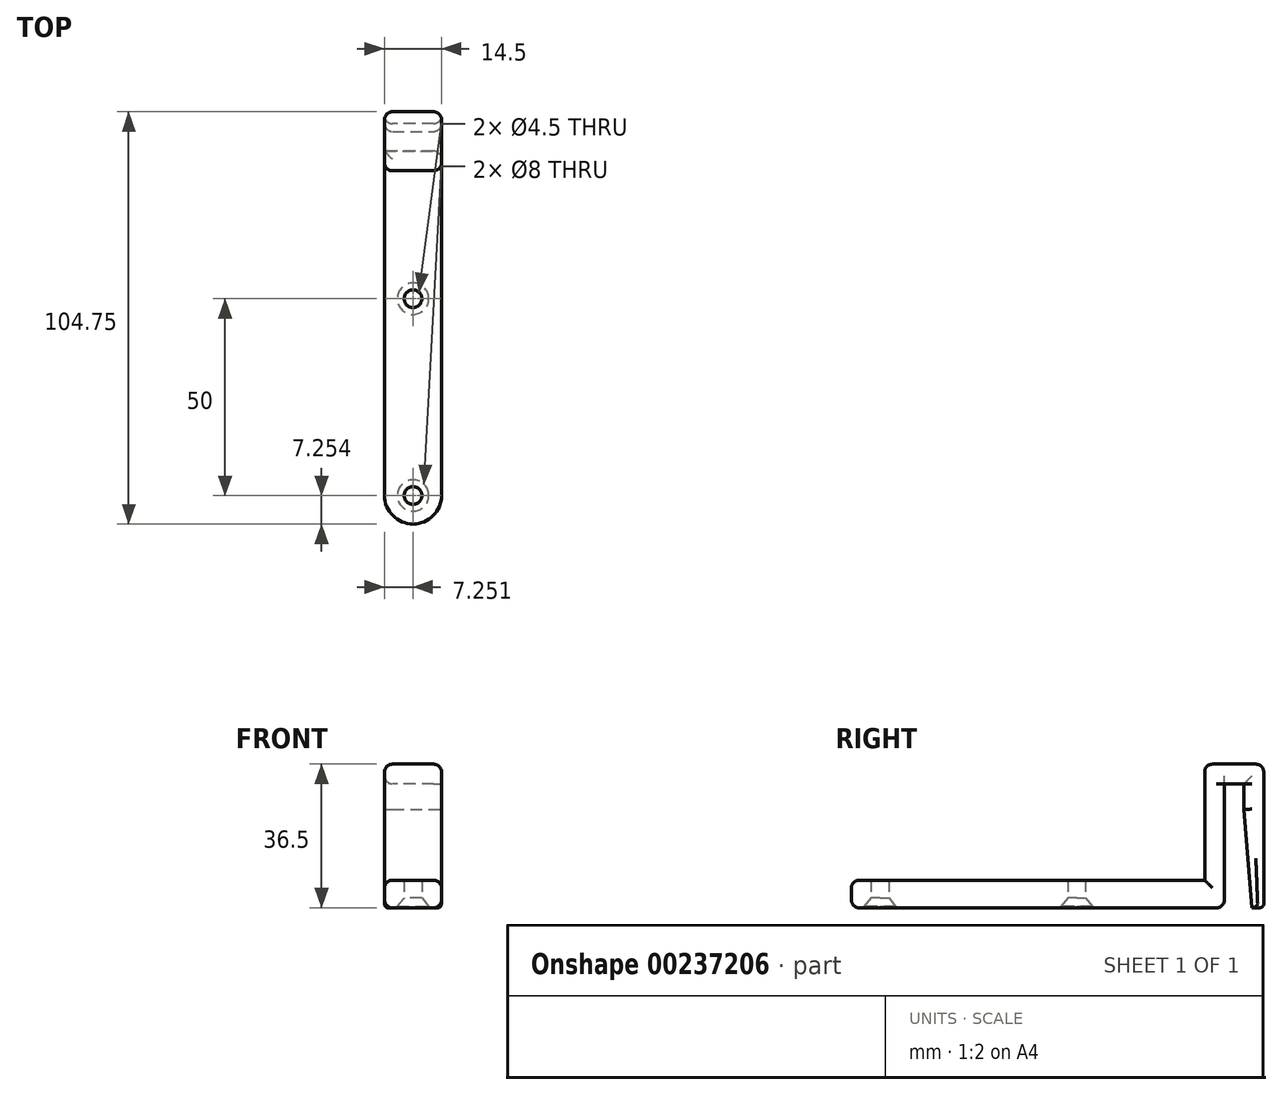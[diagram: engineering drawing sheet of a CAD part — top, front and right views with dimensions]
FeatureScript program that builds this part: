
annotation { "Feature Type Name" : "Feature", "Feature Type Description" : "" }
export const myFeature = defineFeature(function(context is Context, id is Id, definition is map)
    precondition{}
    {
        {
            assignVariable(context, id + "F0", {"name" : "M4_clearance_diameter", "anyValue" : 4.5});
        }
        {
            assignVariable(context, id + "F1", {"name" : "side_thickness", "anyValue" : 5});
        }
        {
            var Q0;
            Q0=qCreatedBy(makeId("Top.planeOp"),FACE);
            var sketch = newSketch(context, id + "F2", { "sketchPlane" : qUnion([Q0])});
            skCircle(sketch, "E0", {"center": v(-10.53, -5.15) * mm, "radius": 2.25 * mm});
            skLineSegment(sketch, "E1.bottom", {"start": v(-17.78, 52.1) * mm, "end": v(-3.28, 52.1) * mm});
            skLineSegment(sketch, "E1.top", {"start": v(-17.78, -12.4) * mm, "end": v(-3.28, -12.4) * mm});
            skLineSegment(sketch, "E1.left", {"start": v(-17.78, 52.1) * mm, "end": v(-17.78, -12.4) * mm});
            skLineSegment(sketch, "E1.right", {"start": v(-3.28, 52.1) * mm, "end": v(-3.28, -12.4) * mm});
            skCircle(sketch, "E2", {"center": v(-10.53, 44.85) * mm, "radius": 2.25 * mm});
            skCircle(sketch, "E3", {"center": v(-10.53, -5.15) * mm, "radius": 7.25 * mm});
            skSolve(sketch);
        }
        {
            assignVariable(context, id + "F3", {"name" : "hole_depth_psu", "anyValue" : 3});
        }
        {
            assignVariable(context, id + "F4", {"name" : "screw_length", "anyValue" : 7.5});
        }
        {
            assignVariable(context, id + "F5", {"name" : "screw_head_length", "anyValue" : 2.5});
        }
        {
            assignVariable(context, id + "F6", {"name" : "bracket_thickness", "anyValue" : getVariable(context, 'screw_length') + getVariable(context, 'screw_head_length') - getVariable(context, 'hole_depth_psu')});
        }
        {
            var Q0;
            {var subQ0=sQuery(id+"F2.wireOp",EDGE,"E1.bottom");Q0=makeQuery(id+"F2.imprint","IMPRINT",FACE,{"disambiguationData":[TD([[makeQuery(id+"F2.imprint","IMPRINT",EDGE,{"derivedFrom":subQ0}),-1.0]])]});}
            var Q1;
            Q1=makeQuery(id+"F2.imprint","IMPRINT",FACE,{"disambiguationData":[TD([[makeQuery(id+"F2.imprint","IMPRINT",EDGE,{"derivedFrom":sQuery(id+"F2.wireOp",EDGE,"E0")}),-1.0]])]});
            extrude(context, id + "F7", {"entities" : qUnion([Q0, Q1]), "depth" : (getVariable(context, 'bracket_thickness')) * mm});
        }
        {
            assignVariable(context, id + "F8", {"name" : "screw_head_diameter", "anyValue" : 8});
        }
        {
            assignVariable(context, id + "F9", {"name" : "screw_head_chamfer", "anyValue" : getVariable(context, 'screw_head_length') - 0.4});
        }
        {
            var Q0;
            Q0=makeQuery(id+"F7.opExtrude","CAP_FACE",FACE,{"disambiguationData":[OSD([sQuery(id+"F2.wireOp",EDGE,"E0"),sQuery(id+"F2.wireOp",EDGE,"E1.bottom"),sQuery(id+"F2.wireOp",EDGE,"E1.left"),sQuery(id+"F2.wireOp",EDGE,"E1.right"),sQuery(id+"F2.wireOp",EDGE,"E2"),sQuery(id+"F2.wireOp",EDGE,"E3")])],"isStart":true});
            var sketch = newSketch(context, id + "F10", { "sketchPlane" : qUnion([Q0])});
            skCircle(sketch, "E4", {"center": v(-10.53, 5.15) * mm, "radius": 4 * mm});
            skCircle(sketch, "E5", {"center": v(-10.53, -44.85) * mm, "radius": 4 * mm});
            skSolve(sketch);
        }
        {
            var Q0;
            Q0=makeQuery(id+"F10.imprint","IMPRINT",FACE,{"disambiguationData":[TD([[makeQuery(id+"F10.imprint","IMPRINT",EDGE,{"derivedFrom":sQuery(id+"F10.wireOp",EDGE,"E4")}),1.0]])]});
            var Q1;
            Q1=makeQuery(id+"F10.imprint","IMPRINT",FACE,{"disambiguationData":[TD([[makeQuery(id+"F10.imprint","IMPRINT",EDGE,{"derivedFrom":sQuery(id+"F10.wireOp",EDGE,"E5")}),1.0]])]});
            extrude(context, id + "F11", {"entities" : qUnion([Q0, Q1]), "operationType" : NewBodyOperationType.REMOVE, "oppositeDirection" : true, "depth" : (getVariable(context, 'screw_head_length')) * mm});
        }
        {
            var Q0;
            Q0=makeQuery(id+"F11.boolean.opBoolean","COPY",EDGE,{"derivedFrom":makeQuery(id+"F11.opExtrude","CAP_EDGE",EDGE,{"disambiguationData":[OSD([sQuery(id+"F10.wireOp",EDGE,"E4")])],"isStart":false})});
            var Q1;
            Q1=makeQuery(id+"F11.boolean.opBoolean","COPY",EDGE,{"derivedFrom":makeQuery(id+"F11.opExtrude","CAP_EDGE",EDGE,{"disambiguationData":[OSD([sQuery(id+"F10.wireOp",EDGE,"E5")])],"isStart":false})});
            chamfer(context, id + "F12", {"entities" : qUnion([Q0, Q1]), "chamferType" : ChamferType.TWO_OFFSETS, "width1" : ((getVariable(context, 'screw_head_diameter') - getVariable(context, 'M4_clearance_diameter')) / 2) * mm, "oppositeDirection" : false, "width2" : (getVariable(context, 'screw_head_chamfer')) * mm, "tangentPropagation" : true});
        }
        {
            assignVariable(context, id + "F13", {"name" : "bracket_height", "anyValue" : 36.5});
        }
        {
            var Q0;
            Q0=makeQuery(id+"F7.opExtrude","CAP_FACE",FACE,{"disambiguationData":[OSD([sQuery(id+"F2.wireOp",EDGE,"E0"),sQuery(id+"F2.wireOp",EDGE,"E1.bottom"),sQuery(id+"F2.wireOp",EDGE,"E1.left"),sQuery(id+"F2.wireOp",EDGE,"E1.right"),sQuery(id+"F2.wireOp",EDGE,"E2"),sQuery(id+"F2.wireOp",EDGE,"E3")])],"isStart":false});
            var sketch = newSketch(context, id + "F14", { "sketchPlane" : qUnion([Q0])});
            skLineSegment(sketch, "E6.bottom", {"start": v(-17.78, 44.85) * mm, "end": v(-3.28, 44.85) * mm});
            skLineSegment(sketch, "E6.top", {"start": v(-17.78, 77.35) * mm, "end": v(-3.28, 77.35) * mm});
            skLineSegment(sketch, "E6.left", {"start": v(-17.78, 44.85) * mm, "end": v(-17.78, 77.35) * mm});
            skLineSegment(sketch, "E6.right", {"start": v(-3.28, 44.85) * mm, "end": v(-3.28, 77.35) * mm});
            skPoint(sketch, "E7", {"position": v(-10.53, 44.85) * mm});
            skSolve(sketch);
        }
        {
            var Q0;
            {var subQ0=sQuery(id+"F14.wireOp",EDGE,"E6.top");Q0=makeQuery(id+"F14.imprint","IMPRINT",FACE,{"disambiguationData":[TD([[makeQuery(id+"F14.imprint","IMPRINT",EDGE,{"derivedFrom":subQ0}),-1.0]])]});}
            extrude(context, id + "F15", {"entities" : qUnion([Q0]), "operationType" : NewBodyOperationType.ADD, "oppositeDirection" : true, "depth" : (getVariable(context, 'bracket_thickness')) * mm});
        }
        {
            var Q0;
            Q0=makeQuery(id+"F15.opExtrude","SWEPT_FACE",FACE,{"disambiguationData":[OSD([sQuery(id+"F14.wireOp",EDGE,"E6.top")])]});
            var sketch = newSketch(context, id + "F16", { "sketchPlane" : qUnion([Q0])});
            skLineSegment(sketch, "E8.bottom", {"start": v(3.28, 0) * mm, "end": v(17.78, 0) * mm});
            skLineSegment(sketch, "E8.top", {"start": v(3.28, 36.5) * mm, "end": v(17.78, 36.5) * mm});
            skLineSegment(sketch, "E8.left", {"start": v(3.28, 0) * mm, "end": v(3.28, 36.5) * mm});
            skLineSegment(sketch, "E8.right", {"start": v(17.78, 0) * mm, "end": v(17.78, 36.5) * mm});
            skSolve(sketch);
        }
        {
            var Q0;
            {var subQ0=sQuery(id+"F16.wireOp",EDGE,"E8.top");Q0=makeQuery(id+"F16.imprint","IMPRINT",FACE,{"disambiguationData":[TD([[makeQuery(id+"F16.imprint","IMPRINT",EDGE,{"derivedFrom":subQ0}),-1.0]])]});}
            var Q1;
            {var subQ0=sQuery(id+"F16.wireOp",EDGE,"E8.bottom");Q1=makeQuery(id+"F16.imprint","IMPRINT",FACE,{"disambiguationData":[TD([[makeQuery(id+"F16.imprint","IMPRINT",EDGE,{"derivedFrom":subQ0}),-1.0]])]});}
            extrude(context, id + "F17", {"entities" : qUnion([Q0, Q1]), "operationType" : NewBodyOperationType.ADD, "depth" : (getVariable(context, 'side_thickness')) * mm});
        }
        {
            var Q0;
            Q0=makeQuery(id+"F17.opExtrude","CAP_FACE",FACE,{"disambiguationData":[OSD([sQuery(id+"F16.wireOp",EDGE,"E8.bottom"),sQuery(id+"F16.wireOp",EDGE,"E8.top"),sQuery(id+"F16.wireOp",EDGE,"E8.left"),sQuery(id+"F16.wireOp",EDGE,"E8.right")])],"isStart":false});
            var sketch = newSketch(context, id + "F18", { "sketchPlane" : qUnion([Q0])});
            skLineSegment(sketch, "E9.bottom", {"start": v(3.28, 36.5) * mm, "end": v(17.78, 36.5) * mm});
            skLineSegment(sketch, "E9.top", {"start": v(3.28, 31.5) * mm, "end": v(17.78, 31.5) * mm});
            skLineSegment(sketch, "E9.left", {"start": v(3.28, 36.5) * mm, "end": v(3.28, 31.5) * mm});
            skLineSegment(sketch, "E9.right", {"start": v(17.78, 36.5) * mm, "end": v(17.78, 31.5) * mm});
            skSolve(sketch);
        }
        {
            var Q0;
            Q0=makeQuery(id+"F18.imprint","IMPRINT",FACE,{"disambiguationData":[TD([[makeQuery(id+"F18.imprint","IMPRINT",EDGE,{"derivedFrom":sQuery(id+"F18.wireOp",EDGE,"E9.bottom")}),-1.0]])]});
            extrude(context, id + "F19", {"entities" : qUnion([Q0]), "operationType" : NewBodyOperationType.ADD, "depth" : 10 * mm});
        }
        {
            var Q0;
            Q0=makeQuery(id+"F19.opExtrude","SWEPT_FACE",FACE,{"disambiguationData":[OSD([sQuery(id+"F18.wireOp",EDGE,"E9.top")])]});
            var sketch = newSketch(context, id + "F20", { "sketchPlane" : qUnion([Q0])});
            skLineSegment(sketch, "E10.bottom", {"start": v(-17.78, -92.35) * mm, "end": v(-3.28, -92.35) * mm});
            skLineSegment(sketch, "E10.top", {"start": v(-17.78, -87.35) * mm, "end": v(-3.28, -87.35) * mm});
            skLineSegment(sketch, "E10.left", {"start": v(-17.78, -92.35) * mm, "end": v(-17.78, -87.35) * mm});
            skLineSegment(sketch, "E10.right", {"start": v(-3.28, -92.35) * mm, "end": v(-3.28, -87.35) * mm});
            skSolve(sketch);
        }
        {
            var Q0;
            Q0=makeQuery(id+"F20.imprint","IMPRINT",FACE,{"disambiguationData":[TD([[makeQuery(id+"F20.imprint","IMPRINT",EDGE,{"derivedFrom":sQuery(id+"F20.wireOp",EDGE,"E10.bottom")}),-1.0]])]});
            extrude(context, id + "F21", {"entities" : qUnion([Q0]), "operationType" : NewBodyOperationType.ADD, "depth" : (getVariable(context, 'bracket_height') - 5) * mm});
        }
        {
            var Q0;
            Q0=makeQuery(id+"F21.opExtrude","CAP_EDGE",EDGE,{"disambiguationData":[OSD([sQuery(id+"F20.wireOp",EDGE,"E10.top")])],"isStart":false});
            chamfer(context, id + "F22", {"entities" : qUnion([Q0]), "chamferType" : ChamferType.TWO_OFFSETS, "width1" : 25 * mm, "oppositeDirection" : false, "width2" : 2 * mm, "tangentPropagation" : true});
        }
        {
            var Q0;
            Q0=makeQuery(id+"F19.boolean.opBoolean","MERGE",EDGE,{"derivedFrom":[makeQuery(id+"F17.opExtrude","SWEPT_EDGE",EDGE,{"disambiguationData":[OSD([sQuery(id+"F16.wireOp",EDGE,"E8.top"),sQuery(id+"F16.wireOp",EDGE,"E8.left")])]}),makeQuery(id+"F19.opExtrude","SWEPT_EDGE",EDGE,{"disambiguationData":[OSD([sQuery(id+"F18.wireOp",EDGE,"E9.bottom"),sQuery(id+"F18.wireOp",EDGE,"E9.left")])]})]});
            var Q1;
            Q1=makeQuery(id+"F17.opExtrude","CAP_EDGE",EDGE,{"disambiguationData":[OSD([sQuery(id+"F16.wireOp",EDGE,"E8.left")])],"isStart":true});
            var Q2;
            Q2=makeQuery(id+"F17.opExtrude","CAP_EDGE",EDGE,{"disambiguationData":[OSD([sQuery(id+"F16.wireOp",EDGE,"E8.left")])],"isStart":false});
            var Q3;
            Q3=makeQuery(id+"F21.opExtrude","SWEPT_EDGE",EDGE,{"disambiguationData":[OSD([sQuery(id+"F16.wireOp",EDGE,"E8.left"),sQuery(id+"F18.wireOp",EDGE,"E9.top"),sQuery(id+"F18.wireOp",EDGE,"E9.left"),sQuery(id+"F20.wireOp",EDGE,"E10.top"),sQuery(id+"F20.wireOp",EDGE,"E10.right")])]});
            var Q4;
            Q4=makeQuery(id+"F21.boolean.opBoolean","MERGE",EDGE,{"derivedFrom":[makeQuery(id+"F19.opExtrude","CAP_EDGE",EDGE,{"disambiguationData":[OSD([sQuery(id+"F18.wireOp",EDGE,"E9.left")])],"isStart":false}),makeQuery(id+"F21.opExtrude","SWEPT_EDGE",EDGE,{"disambiguationData":[OSD([sQuery(id+"F20.wireOp",EDGE,"E10.bottom"),sQuery(id+"F20.wireOp",EDGE,"E10.right")])]})]});
            var Q5;
            Q5=makeQuery(id+"F22.opChamfer","BLEND_EDGE",EDGE,{"blendedFrom":[makeQuery(id+"F21.opExtrude","CAP_EDGE",EDGE,{"disambiguationData":[OSD([sQuery(id+"F20.wireOp",EDGE,"E10.top")])],"isStart":false}),makeQuery(id+"F21.boolean.opBoolean","MERGE",FACE,{"derivedFrom":[makeQuery(id+"F19.boolean.opBoolean","MERGE",FACE,{"derivedFrom":[makeQuery(id+"F17.boolean.opBoolean","MERGE",FACE,{"derivedFrom":[makeQuery(id+"F15.boolean.opBoolean","MERGE",FACE,{"derivedFrom":[makeQuery(id+"F7.opExtrude","SWEPT_FACE",FACE,{"disambiguationData":[OSD([sQuery(id+"F2.wireOp",EDGE,"E1.right")])]}),makeQuery(id+"F15.opExtrude","SWEPT_FACE",FACE,{"disambiguationData":[OSD([sQuery(id+"F14.wireOp",EDGE,"E6.right")])]})]}),makeQuery(id+"F17.opExtrude","SWEPT_FACE",FACE,{"disambiguationData":[OSD([sQuery(id+"F16.wireOp",EDGE,"E8.left")])]})]}),makeQuery(id+"F19.opExtrude","SWEPT_FACE",FACE,{"disambiguationData":[OSD([sQuery(id+"F18.wireOp",EDGE,"E9.left")])]})]}),makeQuery(id+"F21.opExtrude","SWEPT_FACE",FACE,{"disambiguationData":[OSD([sQuery(id+"F20.wireOp",EDGE,"E10.right")])]})]})],"blendedInto":[makeQuery(id+"F21.boolean.opBoolean","MERGE",FACE,{"derivedFrom":[makeQuery(id+"F19.boolean.opBoolean","MERGE",FACE,{"derivedFrom":[makeQuery(id+"F17.boolean.opBoolean","MERGE",FACE,{"derivedFrom":[makeQuery(id+"F15.boolean.opBoolean","MERGE",FACE,{"derivedFrom":[makeQuery(id+"F7.opExtrude","SWEPT_FACE",FACE,{"disambiguationData":[OSD([sQuery(id+"F2.wireOp",EDGE,"E1.right")])]}),makeQuery(id+"F15.opExtrude","SWEPT_FACE",FACE,{"disambiguationData":[OSD([sQuery(id+"F14.wireOp",EDGE,"E6.right")])]})]}),makeQuery(id+"F17.opExtrude","SWEPT_FACE",FACE,{"disambiguationData":[OSD([sQuery(id+"F16.wireOp",EDGE,"E8.left")])]})]}),makeQuery(id+"F19.opExtrude","SWEPT_FACE",FACE,{"disambiguationData":[OSD([sQuery(id+"F18.wireOp",EDGE,"E9.left")])]})]}),makeQuery(id+"F21.opExtrude","SWEPT_FACE",FACE,{"disambiguationData":[OSD([sQuery(id+"F20.wireOp",EDGE,"E10.right")])]})]})]});
            var Q6;
            Q6=makeQuery(id+"F15.boolean.opBoolean","MERGE",EDGE,{"derivedFrom":[makeQuery(id+"F7.opExtrude","CAP_EDGE",EDGE,{"disambiguationData":[OSD([sQuery(id+"F2.wireOp",EDGE,"E1.right")])],"isStart":false}),makeQuery(id+"F15.opExtrude","CAP_EDGE",EDGE,{"disambiguationData":[OSD([sQuery(id+"F14.wireOp",EDGE,"E6.right")])],"isStart":true})]});
            var Q7;
            Q7=makeQuery(id+"F17.boolean.opBoolean","MERGE",EDGE,{"derivedFrom":[makeQuery(id+"F15.boolean.opBoolean","MERGE",EDGE,{"derivedFrom":[makeQuery(id+"F7.opExtrude","CAP_EDGE",EDGE,{"disambiguationData":[OSD([sQuery(id+"F2.wireOp",EDGE,"E1.right")])],"isStart":true}),makeQuery(id+"F15.opExtrude","CAP_EDGE",EDGE,{"disambiguationData":[OSD([sQuery(id+"F14.wireOp",EDGE,"E6.right")])],"isStart":false})]}),makeQuery(id+"F17.opExtrude","SWEPT_EDGE",EDGE,{"disambiguationData":[OSD([sQuery(id+"F16.wireOp",EDGE,"E8.bottom"),sQuery(id+"F16.wireOp",EDGE,"E8.left")])]})]});
            var Q8;
            Q8=makeQuery(id+"F17.opExtrude","CAP_EDGE",EDGE,{"disambiguationData":[OSD([sQuery(id+"F16.wireOp",EDGE,"E8.right")])],"isStart":true});
            var Q9;
            Q9=makeQuery(id+"F22.opChamfer","BLEND_EDGE",EDGE,{"blendedFrom":[makeQuery(id+"F21.opExtrude","CAP_EDGE",EDGE,{"disambiguationData":[OSD([sQuery(id+"F20.wireOp",EDGE,"E10.top")])],"isStart":false}),makeQuery(id+"F21.boolean.opBoolean","MERGE",FACE,{"derivedFrom":[makeQuery(id+"F19.boolean.opBoolean","MERGE",FACE,{"derivedFrom":[makeQuery(id+"F17.boolean.opBoolean","MERGE",FACE,{"derivedFrom":[makeQuery(id+"F15.boolean.opBoolean","MERGE",FACE,{"derivedFrom":[makeQuery(id+"F7.opExtrude","SWEPT_FACE",FACE,{"disambiguationData":[OSD([sQuery(id+"F2.wireOp",EDGE,"E1.left")])]}),makeQuery(id+"F15.opExtrude","SWEPT_FACE",FACE,{"disambiguationData":[OSD([sQuery(id+"F14.wireOp",EDGE,"E6.left")])]})]}),makeQuery(id+"F17.opExtrude","SWEPT_FACE",FACE,{"disambiguationData":[OSD([sQuery(id+"F16.wireOp",EDGE,"E8.right")])]})]}),makeQuery(id+"F19.opExtrude","SWEPT_FACE",FACE,{"disambiguationData":[OSD([sQuery(id+"F18.wireOp",EDGE,"E9.right")])]})]}),makeQuery(id+"F21.opExtrude","SWEPT_FACE",FACE,{"disambiguationData":[OSD([sQuery(id+"F20.wireOp",EDGE,"E10.left")])]})]})],"blendedInto":[makeQuery(id+"F21.boolean.opBoolean","MERGE",FACE,{"derivedFrom":[makeQuery(id+"F19.boolean.opBoolean","MERGE",FACE,{"derivedFrom":[makeQuery(id+"F17.boolean.opBoolean","MERGE",FACE,{"derivedFrom":[makeQuery(id+"F15.boolean.opBoolean","MERGE",FACE,{"derivedFrom":[makeQuery(id+"F7.opExtrude","SWEPT_FACE",FACE,{"disambiguationData":[OSD([sQuery(id+"F2.wireOp",EDGE,"E1.left")])]}),makeQuery(id+"F15.opExtrude","SWEPT_FACE",FACE,{"disambiguationData":[OSD([sQuery(id+"F14.wireOp",EDGE,"E6.left")])]})]}),makeQuery(id+"F17.opExtrude","SWEPT_FACE",FACE,{"disambiguationData":[OSD([sQuery(id+"F16.wireOp",EDGE,"E8.right")])]})]}),makeQuery(id+"F19.opExtrude","SWEPT_FACE",FACE,{"disambiguationData":[OSD([sQuery(id+"F18.wireOp",EDGE,"E9.right")])]})]}),makeQuery(id+"F21.opExtrude","SWEPT_FACE",FACE,{"disambiguationData":[OSD([sQuery(id+"F20.wireOp",EDGE,"E10.left")])]})]})]});
            var Q10;
            Q10=makeQuery(id+"F21.opExtrude","SWEPT_EDGE",EDGE,{"disambiguationData":[OSD([sQuery(id+"F16.wireOp",EDGE,"E8.right"),sQuery(id+"F18.wireOp",EDGE,"E9.top"),sQuery(id+"F18.wireOp",EDGE,"E9.right"),sQuery(id+"F20.wireOp",EDGE,"E10.top"),sQuery(id+"F20.wireOp",EDGE,"E10.left")])]});
            var Q11;
            Q11=makeQuery(id+"F19.opExtrude","SWEPT_EDGE",EDGE,{"disambiguationData":[OSD([sQuery(id+"F16.wireOp",EDGE,"E8.right"),sQuery(id+"F18.wireOp",EDGE,"E9.top"),sQuery(id+"F18.wireOp",EDGE,"E9.right")])]});
            var Q12;
            Q12=makeQuery(id+"F19.boolean.opBoolean","MERGE",EDGE,{"derivedFrom":[makeQuery(id+"F17.opExtrude","SWEPT_EDGE",EDGE,{"disambiguationData":[OSD([sQuery(id+"F16.wireOp",EDGE,"E8.top"),sQuery(id+"F16.wireOp",EDGE,"E8.right")])]}),makeQuery(id+"F19.opExtrude","SWEPT_EDGE",EDGE,{"disambiguationData":[OSD([sQuery(id+"F18.wireOp",EDGE,"E9.bottom"),sQuery(id+"F18.wireOp",EDGE,"E9.right")])]})]});
            var Q13;
            Q13=makeQuery(id+"F17.opExtrude","CAP_EDGE",EDGE,{"disambiguationData":[OSD([sQuery(id+"F16.wireOp",EDGE,"E8.top")])],"isStart":true});
            var Q14;
            Q14=makeQuery(id+"F19.opExtrude","CAP_EDGE",EDGE,{"disambiguationData":[OSD([sQuery(id+"F18.wireOp",EDGE,"E9.bottom")])],"isStart":false});
            var Q15;
            Q15=makeQuery(id+"F21.boolean.opBoolean","MERGE",EDGE,{"derivedFrom":[makeQuery(id+"F19.opExtrude","CAP_EDGE",EDGE,{"disambiguationData":[OSD([sQuery(id+"F18.wireOp",EDGE,"E9.right")])],"isStart":false}),makeQuery(id+"F21.opExtrude","SWEPT_EDGE",EDGE,{"disambiguationData":[OSD([sQuery(id+"F20.wireOp",EDGE,"E10.bottom"),sQuery(id+"F20.wireOp",EDGE,"E10.left")])]})]});
            var Q16;
            Q16=makeQuery(id+"F17.opExtrude","CAP_EDGE",EDGE,{"disambiguationData":[OSD([sQuery(id+"F16.wireOp",EDGE,"E8.bottom")])],"isStart":false});
            fillet(context, id + "F23", {"entities" : qUnion([Q0, Q1, Q2, Q3, Q4, Q5, Q6, Q7, Q8, Q9, Q10, Q11, Q12, Q13, Q14, Q15, Q16]), "radius" : 2 * mm, "tangentPropagation" : true, "allowEdgeOverflow" : false});
        }
        {
            var Q0;
            Q0=makeQuery(id+"F21.opExtrude","CAP_EDGE",EDGE,{"disambiguationData":[OSD([sQuery(id+"F20.wireOp",EDGE,"E10.bottom")])],"isStart":false});
            fillet(context, id + "F24", {"entities" : qUnion([Q0]), "radius" : 1 * mm, "tangentPropagation" : true, "allowEdgeOverflow" : false});
        }
    });
